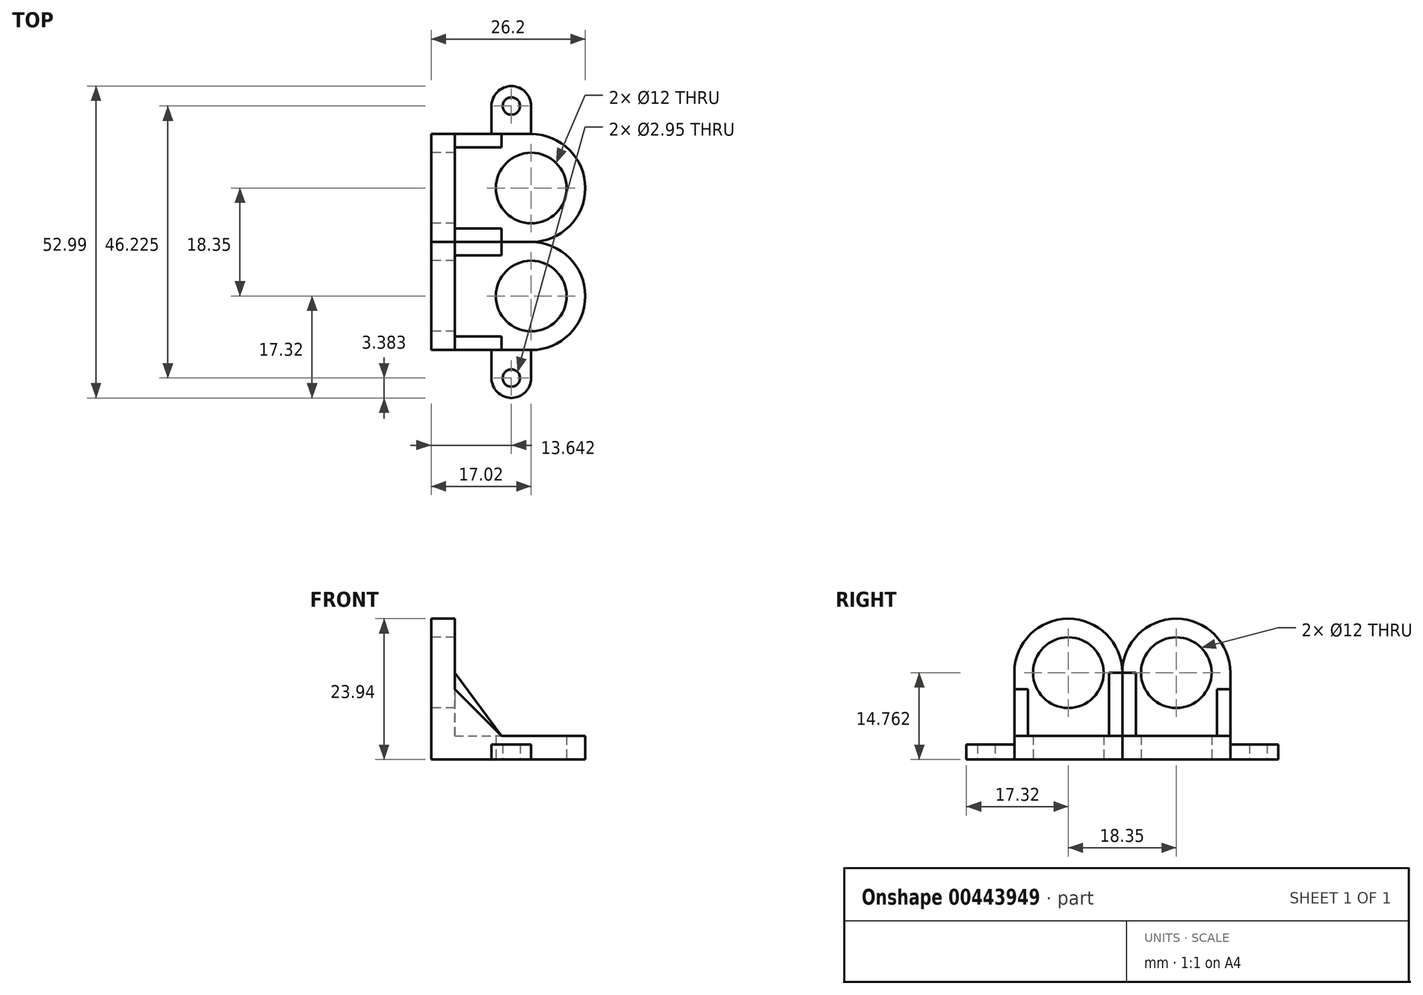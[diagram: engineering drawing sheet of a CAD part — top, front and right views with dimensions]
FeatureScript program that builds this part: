
annotation { "Feature Type Name" : "Feature", "Feature Type Description" : "" }
export const myFeature = defineFeature(function(context is Context, id is Id, definition is map)
    precondition{}
    {
        {
            var Q0;
            Q0=qCreatedBy(makeId("Top.planeOp"),FACE);
            var sketch = newSketch(context, id + "F0", { "sketchPlane" : qUnion([Q0])});
            skCircle(sketch, "E0", {"center": v(0, 0) * mm, "radius": 6 * mm});
            skArc(sketch, "E1", {"start": v(0, 9.18) * mm, "mid": v(9.18, 0) * mm, "end": v(0, -9.18) * mm});
            skLineSegment(sketch, "E2", {"start": v(0, 9.18) * mm, "end": v(-17.02, 9.18) * mm});
            skLineSegment(sketch, "E3", {"start": v(-17.02, 9.17) * mm, "end": v(-17.02, -9.18) * mm});
            skLineSegment(sketch, "E4", {"start": v(-17.02, -9.18) * mm, "end": v(0, -9.18) * mm});
            skSolve(sketch);
        }
        {
            var Q0;
            Q0=qSketchRegion(id+"F0",true);
            extrude(context, id + "F1", {"entities" : qUnion([Q0]), "depth" : 4 * mm});
        }
        {
            var Q0;
            Q0=makeQuery(id+"F1.opExtrude","SWEPT_FACE",FACE,{"disambiguationData":[OSD([sQuery(id+"F0.wireOp",EDGE,"E3")])]});
            var sketch = newSketch(context, id + "F2", { "sketchPlane" : qUnion([Q0])});
            skCircle(sketch, "E5", {"center": v(0, 14.76) * mm, "radius": 6 * mm});
            skArc(sketch, "E6", {"start": v(-9.17, 14.76) * mm, "mid": v(0, 23.94) * mm, "end": v(9.17, 14.76) * mm});
            skLineSegment(sketch, "E7", {"start": v(-9.17, 14.76) * mm, "end": v(-9.18, 4) * mm});
            skLineSegment(sketch, "E8", {"start": v(-9.18, 4) * mm, "end": v(9.18, 4) * mm});
            skLineSegment(sketch, "E9", {"start": v(9.17, 4) * mm, "end": v(9.17, 14.76) * mm});
            skSolve(sketch);
        }
        {
            var Q0;
            Q0=qSketchRegion(id+"F2",true);
            extrude(context, id + "F3", {"entities" : qUnion([Q0]), "operationType" : NewBodyOperationType.ADD, "oppositeDirection" : true, "depth" : 4 * mm});
        }
        {
            var Q0;
            Q0=makeQuery(id+"F3.boolean.opBoolean","MERGE",FACE,{"derivedFrom":[makeQuery(id+"F1.opExtrude","SWEPT_FACE",FACE,{"disambiguationData":[OSD([sQuery(id+"F0.wireOp",EDGE,"E4")])]}),makeQuery(id+"F3.opExtrude","SWEPT_FACE",FACE,{"disambiguationData":[OSD([sQuery(id+"F2.wireOp",EDGE,"E9")])]})]});
            var sketch = newSketch(context, id + "F4", { "sketchPlane" : qUnion([Q0])});
            skLineSegment(sketch, "E10", {"start": v(-13.02, 11.94) * mm, "end": v(-5.08, 4) * mm});
            skLineSegment(sketch, "E11", {"start": v(-5.08, 4) * mm, "end": v(-13.02, 4) * mm});
            skLineSegment(sketch, "E12", {"start": v(-13.02, 4) * mm, "end": v(-13.02, 11.94) * mm});
            skSolve(sketch);
        }
        {
            var Q0;
            Q0=qSketchRegion(id+"F4",true);
            extrude(context, id + "F5", {"entities" : qUnion([Q0]), "operationType" : NewBodyOperationType.ADD, "oppositeDirection" : true, "depth" : 2.3 * mm});
        }
        {
            var Q0;
            Q0=makeQuery(id+"F3.boolean.opBoolean","MERGE",FACE,{"derivedFrom":[makeQuery(id+"F1.opExtrude","SWEPT_FACE",FACE,{"disambiguationData":[OSD([sQuery(id+"F0.wireOp",EDGE,"E2")])]}),makeQuery(id+"F3.opExtrude","SWEPT_FACE",FACE,{"disambiguationData":[OSD([sQuery(id+"F2.wireOp",EDGE,"E7")])]})]});
            var sketch = newSketch(context, id + "F6", { "sketchPlane" : qUnion([Q0])});
            skLineSegment(sketch, "E13", {"start": v(13.02, 14.76) * mm, "end": v(5.08, 4) * mm});
            skLineSegment(sketch, "E14", {"start": v(5.08, 4) * mm, "end": v(13.02, 4) * mm});
            skLineSegment(sketch, "E15", {"start": v(13.02, 4) * mm, "end": v(13.02, 14.76) * mm});
            skSolve(sketch);
        }
        {
            var Q0;
            Q0=qSketchRegion(id+"F6",true);
            extrude(context, id + "F7", {"entities" : qUnion([Q0]), "operationType" : NewBodyOperationType.ADD, "oppositeDirection" : true, "depth" : 2.3 * mm});
        }
        {
            var Q0;
            Q0=makeQuery(id+"F1.opExtrude","CAP_FACE",FACE,{"disambiguationData":[OSD([sQuery(id+"F0.wireOp",EDGE,"E0"),sQuery(id+"F0.wireOp",EDGE,"E1"),sQuery(id+"F0.wireOp",EDGE,"E2"),sQuery(id+"F0.wireOp",EDGE,"E3"),sQuery(id+"F0.wireOp",EDGE,"E4")])],"isStart":true});
            var sketch = newSketch(context, id + "F8", { "sketchPlane" : qUnion([Q0])});
            skCircle(sketch, "E16", {"center": v(-3.38, 13.94) * mm, "radius": 1.47 * mm});
            skArc(sketch, "E17", {"start": v(-6.76, 13.94) * mm, "mid": v(-3.38, 17.32) * mm, "end": v(0, 13.94) * mm});
            skLineSegment(sketch, "E18", {"start": v(-6.76, 13.94) * mm, "end": v(-6.76, 9.18) * mm});
            skLineSegment(sketch, "E19", {"start": v(-6.76, 9.18) * mm, "end": v(0, 9.18) * mm});
            skLineSegment(sketch, "E20", {"start": v(0, 9.18) * mm, "end": v(0, 13.94) * mm});
            skSolve(sketch);
        }
        {
            var Q0;
            Q0=qSketchRegion(id+"F8",true);
            extrude(context, id + "F9", {"entities" : qUnion([Q0]), "operationType" : NewBodyOperationType.ADD, "oppositeDirection" : true, "depth" : 2.54 * mm});
        }
        {
            var Q0;
            Q0=makeQuery(id+"F1.opExtrude","SWEPT_BODY",BODY,{"disambiguationData":[OSD([sQuery(id+"F0.wireOp",EDGE,"E0"),sQuery(id+"F0.wireOp",EDGE,"E1"),sQuery(id+"F0.wireOp",EDGE,"E2"),sQuery(id+"F0.wireOp",EDGE,"E3"),sQuery(id+"F0.wireOp",EDGE,"E4")])]});
            var Q1;
            Q1=makeQuery(id+"F7.boolean.opBoolean","MERGE",FACE,{"derivedFrom":[makeQuery(id+"F3.boolean.opBoolean","MERGE",FACE,{"derivedFrom":[makeQuery(id+"F1.opExtrude","SWEPT_FACE",FACE,{"disambiguationData":[OSD([sQuery(id+"F0.wireOp",EDGE,"E2")])]}),makeQuery(id+"F3.opExtrude","SWEPT_FACE",FACE,{"disambiguationData":[OSD([sQuery(id+"F2.wireOp",EDGE,"E7")])]})]}),makeQuery(id+"F7.opExtrude","CAP_FACE",FACE,{"disambiguationData":[OSD([sQuery(id+"F6.wireOp",EDGE,"E13"),sQuery(id+"F6.wireOp",EDGE,"E14"),sQuery(id+"F6.wireOp",EDGE,"E15")])],"isStart":true})]});
            mirror(context, id + "F10", {"entities" : qUnion([Q0]), "mirrorPlane" : qUnion([Q1])});
        }
    });
